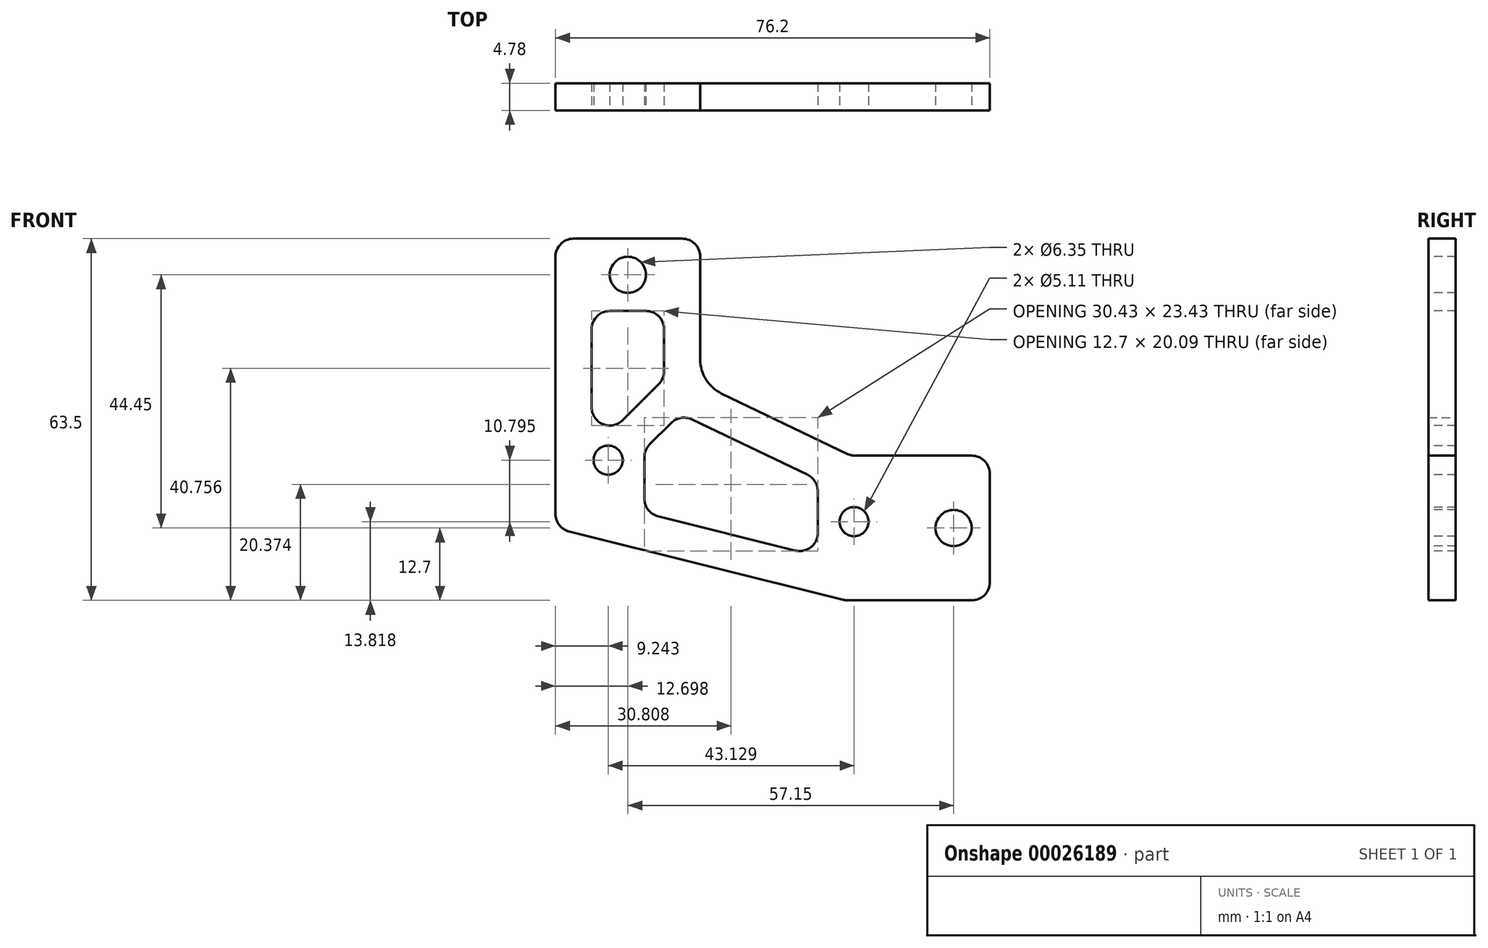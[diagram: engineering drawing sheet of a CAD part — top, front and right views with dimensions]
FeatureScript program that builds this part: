
annotation { "Feature Type Name" : "Feature", "Feature Type Description" : "" }
export const myFeature = defineFeature(function(context is Context, id is Id, definition is map)
    precondition{}
    {
        {
            var Q0;
            Q0=qCreatedBy(makeId("Front.planeOp"),FACE);
            var sketch = newSketch(context, id + "F0", { "sketchPlane" : qUnion([Q0])});
            skLineSegment(sketch, "E0.bottom", {"start": v(-38.85, 38.1) * mm, "end": v(-13.45, 38.1) * mm});
            skLineSegment(sketch, "E0.top", {"start": v(12.08, -25.4) * mm, "end": v(37.35, -25.4) * mm});
            skLineSegment(sketch, "E0.left", {"start": v(-38.85, 38.1) * mm, "end": v(-38.85, -12.7) * mm});
            skLineSegment(sketch, "E0.right", {"start": v(37.35, 0) * mm, "end": v(37.35, -25.4) * mm});
            skLineSegment(sketch, "E1", {"start": v(-38.85, -12.7) * mm, "end": v(12.08, -25.4) * mm});
            skLineSegment(sketch, "E2", {"start": v(-13.45, 38.1) * mm, "end": v(-13.45, 12.7) * mm});
            skLineSegment(sketch, "E3", {"start": v(-13.45, 12.7) * mm, "end": v(13.04, 0) * mm});
            skLineSegment(sketch, "E4", {"start": v(13.04, 0) * mm, "end": v(37.35, 0) * mm});
            skSolve(sketch);
        }
        {
            var Q0;
            Q0=makeQuery(id+"F0.imprint","IMPRINT",FACE,{"disambiguationData":[TD([[makeQuery(id+"F0.imprint","IMPRINT",EDGE,{"derivedFrom":sQuery(id+"F0.wireOp",EDGE,"E0.bottom")}),-1.0]])]});
            extrude(context, id + "F1", {"entities" : qUnion([Q0]), "depth" : 4.78 * mm});
        }
        {
            var Q0;
            Q0=makeQuery(id+"F1.opExtrude","SWEPT_EDGE",EDGE,{"disambiguationData":[OSD([sQuery(id+"F0.wireOp",EDGE,"E0.bottom"),sQuery(id+"F0.wireOp",EDGE,"E0.left")])]});
            var Q1;
            Q1=makeQuery(id+"F1.opExtrude","SWEPT_EDGE",EDGE,{"disambiguationData":[OSD([sQuery(id+"F0.wireOp",EDGE,"E0.left"),sQuery(id+"F0.wireOp",EDGE,"E1")])]});
            var Q2;
            Q2=makeQuery(id+"F1.opExtrude","SWEPT_EDGE",EDGE,{"disambiguationData":[OSD([sQuery(id+"F0.wireOp",EDGE,"E0.top"),sQuery(id+"F0.wireOp",EDGE,"E0.right")])]});
            var Q3;
            Q3=makeQuery(id+"F1.opExtrude","SWEPT_EDGE",EDGE,{"disambiguationData":[OSD([sQuery(id+"F0.wireOp",EDGE,"E0.right"),sQuery(id+"F0.wireOp",EDGE,"E4")])]});
            var Q4;
            Q4=makeQuery(id+"F1.opExtrude","SWEPT_EDGE",EDGE,{"disambiguationData":[OSD([sQuery(id+"F0.wireOp",EDGE,"E0.top"),sQuery(id+"F0.wireOp",EDGE,"E1")])]});
            var Q5;
            Q5=makeQuery(id+"F1.opExtrude","SWEPT_EDGE",EDGE,{"disambiguationData":[OSD([sQuery(id+"F0.wireOp",EDGE,"E0.bottom"),sQuery(id+"F0.wireOp",EDGE,"E2")])]});
            var Q6;
            Q6=makeQuery(id+"F1.opExtrude","SWEPT_EDGE",EDGE,{"disambiguationData":[OSD([sQuery(id+"F0.wireOp",EDGE,"E3"),sQuery(id+"F0.wireOp",EDGE,"E4")])]});
            fillet(context, id + "F2", {"entities" : qUnion([Q0, Q1, Q2, Q3, Q4, Q5, Q6]), "radius" : 3.17 * mm, "tangentPropagation" : true, "allowEdgeOverflow" : false});
        }
        {
            var Q0;
            Q0=makeQuery(id+"F1.opExtrude","SWEPT_EDGE",EDGE,{"disambiguationData":[OSD([sQuery(id+"F0.wireOp",EDGE,"E2"),sQuery(id+"F0.wireOp",EDGE,"E3")])]});
            fillet(context, id + "F3", {"entities" : qUnion([Q0]), "radius" : 6.6 * mm, "tangentPropagation" : true, "allowEdgeOverflow" : false});
        }
        {
            var Q0;
            Q0=makeQuery(id+"F1.opExtrude","CAP_FACE",FACE,{"disambiguationData":[OSD([sQuery(id+"F0.wireOp",EDGE,"E0.bottom"),sQuery(id+"F0.wireOp",EDGE,"E0.top"),sQuery(id+"F0.wireOp",EDGE,"E0.left"),sQuery(id+"F0.wireOp",EDGE,"E0.right"),sQuery(id+"F0.wireOp",EDGE,"E1"),sQuery(id+"F0.wireOp",EDGE,"E2"),sQuery(id+"F0.wireOp",EDGE,"E3"),sQuery(id+"F0.wireOp",EDGE,"E4")])],"isStart":false});
            var sketch = newSketch(context, id + "F4", { "sketchPlane" : qUnion([Q0])});
            skLineSegment(sketch, "E5.0", {"start": v(-19.8, 13.5) * mm, "end": v(-19.8, 25.4) * mm});
            skLineSegment(sketch, "E5.2", {"start": v(7.17, -4.23) * mm, "end": v(-16.98, 7.35) * mm});
            skLineSegment(sketch, "E5.8", {"start": v(-23.26, -10.04) * mm, "end": v(7.17, -17.63) * mm});
            skLineSegment(sketch, "E5.9", {"start": v(-32.5, 25.4) * mm, "end": v(-32.5, 0.8) * mm});
            skLineSegment(sketch, "E6", {"start": v(-19.8, 13.5) * mm, "end": v(-32.5, 0.8) * mm});
            skLineSegment(sketch, "E7", {"start": v(-16.98, 7.35) * mm, "end": v(-23.26, 1.07) * mm});
            skLineSegment(sketch, "E8", {"start": v(-23.26, 1.07) * mm, "end": v(-23.26, -10.04) * mm});
            skLineSegment(sketch, "E9", {"start": v(7.17, -4.23) * mm, "end": v(7.17, -17.63) * mm});
            skLineSegment(sketch, "E10", {"start": v(-32.5, 25.4) * mm, "end": v(-19.8, 25.4) * mm});
            skCircle(sketch, "E11", {"center": v(-26.15, 31.75) * mm, "radius": 3.18 * mm});
            skCircle(sketch, "E12", {"center": v(13.52, -11.58) * mm, "radius": 2.55 * mm});
            skCircle(sketch, "E13", {"center": v(-29.6, -0.79) * mm, "radius": 2.55 * mm});
            skCircle(sketch, "E14", {"center": v(31, -12.7) * mm, "radius": 3.18 * mm});
            skLineSegment(sketch, "E15", {"start": v(-29.6, -0.79) * mm, "end": v(-16.14, 12.68) * mm, "construction": true});
            skSolve(sketch);
        }
        {
            var Q0;
            Q0=makeQuery(id+"F4.imprint","IMPRINT",FACE,{"disambiguationData":[TD([[makeQuery(id+"F4.imprint","IMPRINT",EDGE,{"derivedFrom":sQuery(id+"F4.wireOp",EDGE,"E11")}),1.0]])]});
            var Q1;
            Q1=makeQuery(id+"F4.imprint","IMPRINT",FACE,{"disambiguationData":[TD([[makeQuery(id+"F4.imprint","IMPRINT",EDGE,{"derivedFrom":sQuery(id+"F4.wireOp",EDGE,"E5.0")}),1.0]])]});
            var Q2;
            Q2=makeQuery(id+"F4.imprint","IMPRINT",FACE,{"disambiguationData":[TD([[makeQuery(id+"F4.imprint","IMPRINT",EDGE,{"derivedFrom":sQuery(id+"F4.wireOp",EDGE,"E13")}),1.0]])]});
            var Q3;
            Q3=makeQuery(id+"F4.imprint","IMPRINT",FACE,{"disambiguationData":[TD([[makeQuery(id+"F4.imprint","IMPRINT",EDGE,{"derivedFrom":sQuery(id+"F4.wireOp",EDGE,"E5.2")}),1.0]])]});
            var Q4;
            Q4=makeQuery(id+"F4.imprint","IMPRINT",FACE,{"disambiguationData":[TD([[makeQuery(id+"F4.imprint","IMPRINT",EDGE,{"derivedFrom":sQuery(id+"F4.wireOp",EDGE,"E12")}),1.0]])]});
            var Q5;
            Q5=makeQuery(id+"F4.imprint","IMPRINT",FACE,{"disambiguationData":[TD([[makeQuery(id+"F4.imprint","IMPRINT",EDGE,{"derivedFrom":sQuery(id+"F4.wireOp",EDGE,"E14")}),1.0]])]});
            extrude(context, id + "F5", {"entities" : qUnion([Q0, Q1, Q2, Q3, Q4, Q5]), "operationType" : NewBodyOperationType.REMOVE, "endBound" : BoundingType.THROUGH_ALL, "oppositeDirection" : true, "depth" : 25.4 * mm});
        }
        {
            var Q0;
            Q0=makeQuery(id+"F5.boolean.opBoolean","COPY",EDGE,{"derivedFrom":makeQuery(id+"F5.opExtrude","SWEPT_EDGE",EDGE,{"disambiguationData":[OSD([sQuery(id+"F4.wireOp",EDGE,"E5.9"),sQuery(id+"F4.wireOp",EDGE,"E10")])]})});
            var Q1;
            Q1=makeQuery(id+"F5.boolean.opBoolean","COPY",EDGE,{"derivedFrom":makeQuery(id+"F5.opExtrude","SWEPT_EDGE",EDGE,{"disambiguationData":[OSD([sQuery(id+"F4.wireOp",EDGE,"E5.0"),sQuery(id+"F4.wireOp",EDGE,"E10")])]})});
            var Q2;
            Q2=makeQuery(id+"F5.boolean.opBoolean","COPY",EDGE,{"derivedFrom":makeQuery(id+"F5.opExtrude","SWEPT_EDGE",EDGE,{"disambiguationData":[OSD([sQuery(id+"F4.wireOp",EDGE,"E5.9"),sQuery(id+"F4.wireOp",EDGE,"E6")])]})});
            var Q3;
            Q3=makeQuery(id+"F5.boolean.opBoolean","COPY",EDGE,{"derivedFrom":makeQuery(id+"F5.opExtrude","SWEPT_EDGE",EDGE,{"disambiguationData":[OSD([sQuery(id+"F4.wireOp",EDGE,"E5.0"),sQuery(id+"F4.wireOp",EDGE,"E6")])]})});
            var Q4;
            Q4=makeQuery(id+"F5.boolean.opBoolean","COPY",EDGE,{"derivedFrom":makeQuery(id+"F5.opExtrude","SWEPT_EDGE",EDGE,{"disambiguationData":[OSD([sQuery(id+"F4.wireOp",EDGE,"E5.2"),sQuery(id+"F4.wireOp",EDGE,"E7")])]})});
            var Q5;
            Q5=makeQuery(id+"F5.boolean.opBoolean","COPY",EDGE,{"derivedFrom":makeQuery(id+"F5.opExtrude","SWEPT_EDGE",EDGE,{"disambiguationData":[OSD([sQuery(id+"F4.wireOp",EDGE,"E7"),sQuery(id+"F4.wireOp",EDGE,"E8")])]})});
            var Q6;
            Q6=makeQuery(id+"F5.boolean.opBoolean","COPY",EDGE,{"derivedFrom":makeQuery(id+"F5.opExtrude","SWEPT_EDGE",EDGE,{"disambiguationData":[OSD([sQuery(id+"F4.wireOp",EDGE,"E5.8"),sQuery(id+"F4.wireOp",EDGE,"E8")])]})});
            var Q7;
            Q7=makeQuery(id+"F5.boolean.opBoolean","COPY",EDGE,{"derivedFrom":makeQuery(id+"F5.opExtrude","SWEPT_EDGE",EDGE,{"disambiguationData":[OSD([sQuery(id+"F4.wireOp",EDGE,"E5.2"),sQuery(id+"F4.wireOp",EDGE,"E9")])]})});
            var Q8;
            Q8=makeQuery(id+"F5.boolean.opBoolean","COPY",EDGE,{"derivedFrom":makeQuery(id+"F5.opExtrude","SWEPT_EDGE",EDGE,{"disambiguationData":[OSD([sQuery(id+"F4.wireOp",EDGE,"E5.8"),sQuery(id+"F4.wireOp",EDGE,"E9")])]})});
            fillet(context, id + "F6", {"entities" : qUnion([Q0, Q1, Q2, Q3, Q4, Q5, Q6, Q7, Q8]), "radius" : 3.17 * mm, "tangentPropagation" : true, "allowEdgeOverflow" : false});
        }
    });
